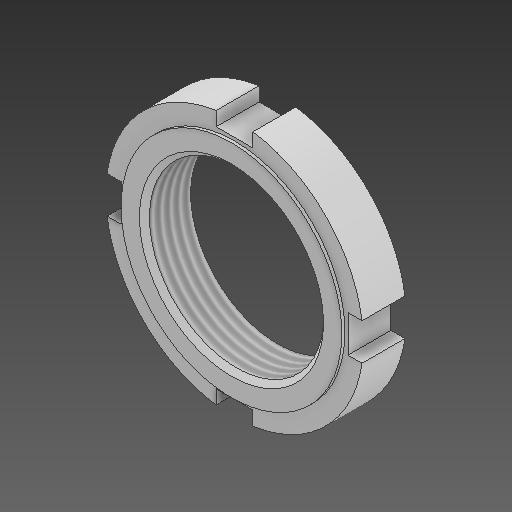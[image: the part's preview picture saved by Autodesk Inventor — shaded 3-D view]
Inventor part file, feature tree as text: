
AUTODESK INVENTOR PART (.ipt)
format: ipt  version: 2021 (Build 250183000, 183)  size: 199,168 bytes
history: native  units: in
note: dims shown in document units (in); Inventor stores cm internally (conversion verified against a paired STEP export)
features: other x19, sketch x4
ambient origin geometry x8: Origin, YZ Plane, XZ Plane, XY Plane, X Axis, Y Axis, Z Axis, Center Point
bodies: Solid1 (feature_tree)
feature tree (23):
  other  "3753 M30x1_5.ipt"
  other  "Solid1::3753 M30x1_5.ipt"
  other  "TaggingFeature1"
  sketch  "Sketch_1"  dims[d0=0.3937in]
  sketch  "Sketch_2"  dims[d7=0.0in d8=0.0in]
  sketch  "Sketch_6"
  sketch  "Sketch_3"
  other  "FDT_CYLINDER_XY"
  other  "FDT_CYLINDER_YZ"
  other  "FDT_CYLINDER_ZX"
  other  "NUT_XY"
  other  "NUT_YZ"
  other  "NUT_ZX"
  other  "FDT_CYLINDER_X"
  other  "FDT_CYLINDER_Y"
  other  "FDT_CYLINDER_Z"
  other  "NUT_X"
  other  "NUT_Y"
  other  "NUT_Z"
  other  "FDT_CYLINDER_Center"
  other  "NUT_Center"
  other  "NUT"
  other  "FDT_CYLINDER"
